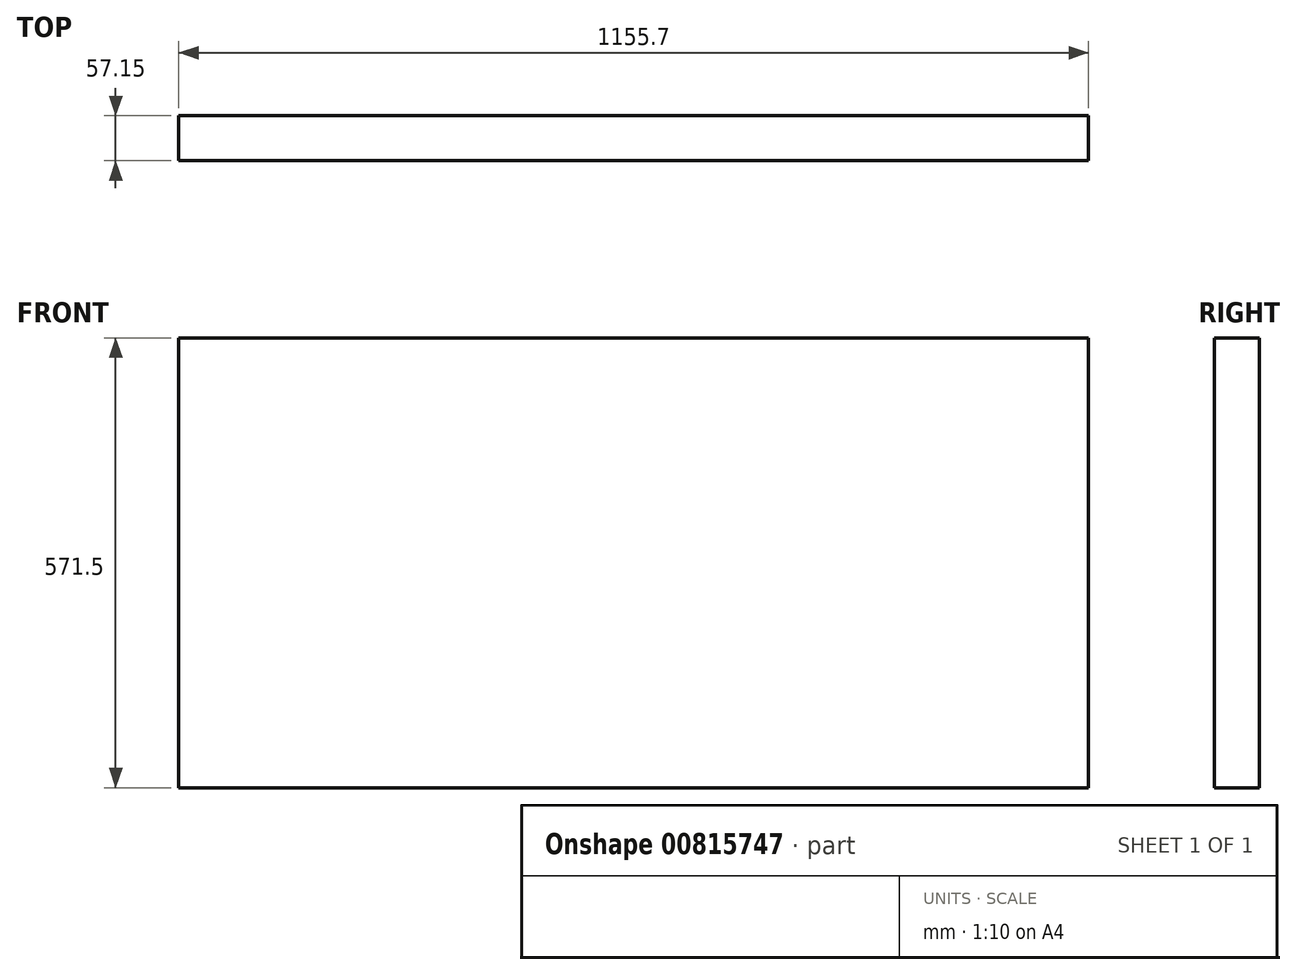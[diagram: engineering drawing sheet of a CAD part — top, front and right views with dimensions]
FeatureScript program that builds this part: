
annotation { "Feature Type Name" : "Feature", "Feature Type Description" : "" }
export const myFeature = defineFeature(function(context is Context, id is Id, definition is map)
    precondition{}
    {
        {
            var Q0;
            Q0=qCreatedBy(makeId("Front.planeOp"),FACE);
            var sketch = newSketch(context, id + "F0", { "sketchPlane" : qUnion([Q0])});
            skLineSegment(sketch, "E0.bottom", {"start": v(590.55, 288.16) * mm, "end": v(-590.55, 288.16) * mm});
            skLineSegment(sketch, "E0.top", {"start": v(590.55, -283.34) * mm, "end": v(-590.55, -283.34) * mm});
            skLineSegment(sketch, "E0.left", {"start": v(590.55, 288.16) * mm, "end": v(590.55, -283.34) * mm});
            skLineSegment(sketch, "E0.right", {"start": v(-590.55, 288.16) * mm, "end": v(-590.55, -283.34) * mm});
            skPoint(sketch, "E0.middle", {"position": v(0, 2.4) * mm});
            skSolve(sketch);
        }
        {
            var Q0;
            Q0 = qSketchRegion(id + "F0", true);
            extrude(context, id + "F1", {"entities" : qUnion([Q0]), "depth" : 50.8 * mm, "offsetDistance" : 25.4 * mm});
        }
        {
            var Q0;
            Q0=makeQuery(id+"F1.opExtrude","SWEPT_FACE",FACE,{"disambiguationData":[OSD([sQuery(id+"F0.wireOp",EDGE,"E0.right")])]});
            extrude(context, id + "F2", {"entities" : qUnion([Q0]), "operationType" : NewBodyOperationType.REMOVE, "oppositeDirection" : true, "depth" : 25.4 * mm, "offsetDistance" : 25.4 * mm});
        }
        {
            var Q0;
            Q0=makeQuery(id+"F1.opExtrude","CAP_FACE",FACE,{"disambiguationData":[OSD([sQuery(id+"F0.wireOp",EDGE,"E0.bottom"),sQuery(id+"F0.wireOp",EDGE,"E0.top"),sQuery(id+"F0.wireOp",EDGE,"E0.left"),sQuery(id+"F0.wireOp",EDGE,"E0.right")])],"isStart":false});
            extrude(context, id + "F3", {"entities" : qUnion([Q0]), "operationType" : NewBodyOperationType.ADD, "depth" : 6.35 * mm, "offsetDistance" : 25.4 * mm});
        }
    });
